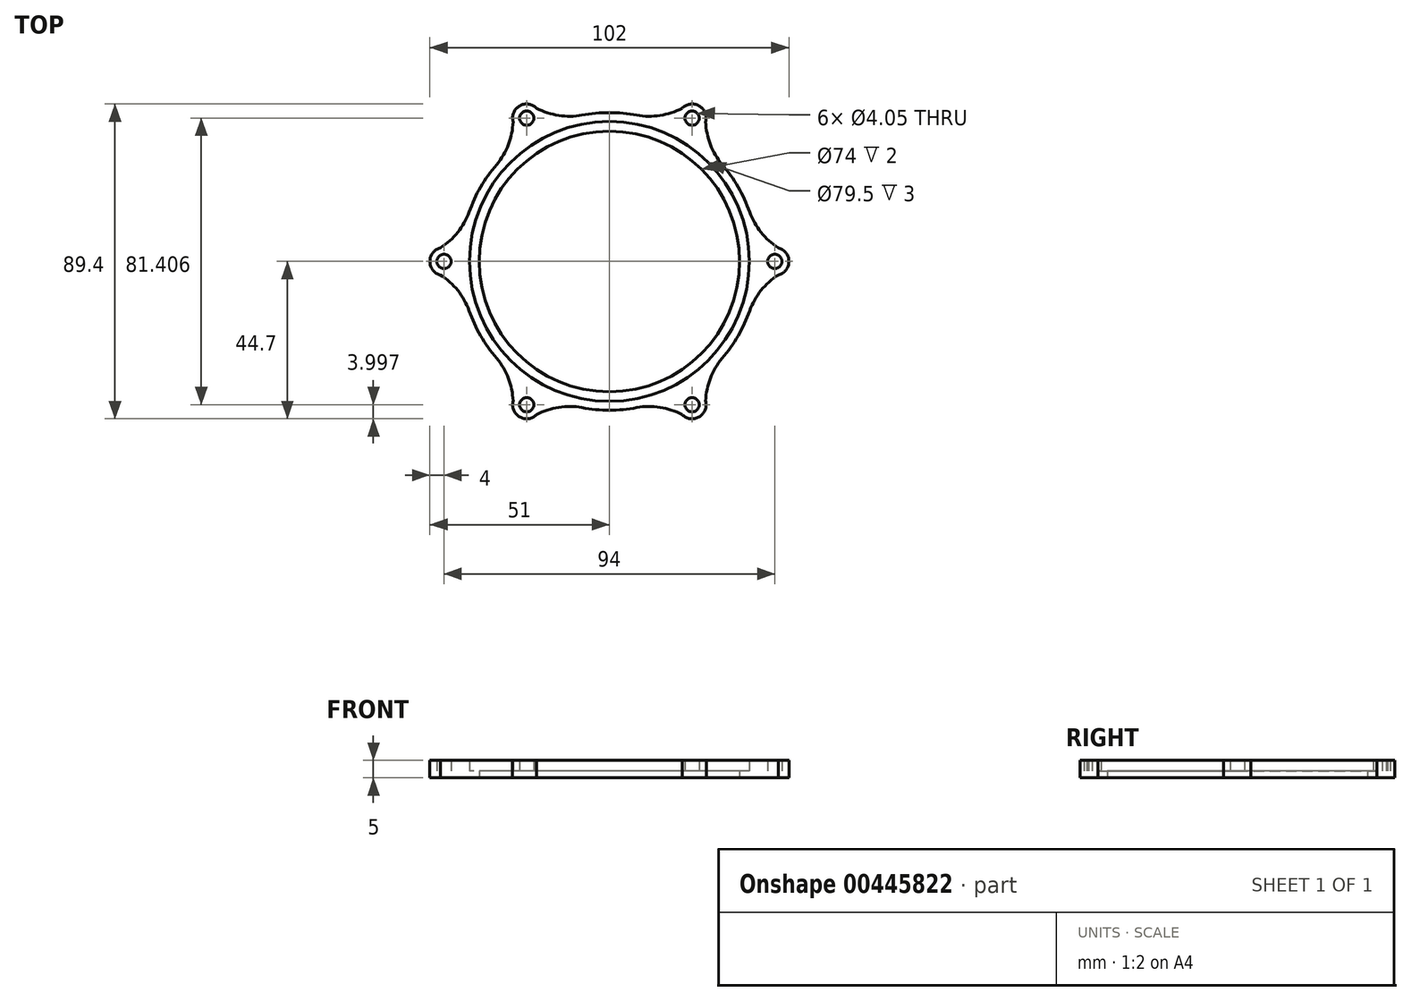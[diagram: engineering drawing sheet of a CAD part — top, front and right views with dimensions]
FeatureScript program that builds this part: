
annotation { "Feature Type Name" : "Feature", "Feature Type Description" : "" }
export const myFeature = defineFeature(function(context is Context, id is Id, definition is map)
    precondition{}
    {
        {
            var Q0;
            Q0=qCreatedBy(makeId("Top.planeOp"),FACE);
            var sketch = newSketch(context, id + "F0", { "sketchPlane" : qUnion([Q0])});
            skCircle(sketch, "E0", {"center": v(0, 0) * mm, "radius": 37 * mm});
            skCircle(sketch, "E1", {"center": v(0, 0) * mm, "radius": 39.75 * mm});
            skArc(sketch, "E2", {"start": v(-32.06, 27.52) * mm, "mid": v(-36.59, 21.12) * mm, "end": v(-39.86, 14) * mm});
            skArc(sketch, "E3", {"start": v(-48, 3.87) * mm, "mid": v(-51, 0) * mm, "end": v(-48, -3.87) * mm});
            skCircle(sketch, "E4", {"center": v(-47, 0) * mm, "radius": 2.02 * mm});
            skArc(sketch, "E5", {"start": v(-48, 3.87) * mm, "mid": v(-43.09, 8.26) * mm, "end": v(-39.86, 14) * mm});
            skArc(sketch, "E6.MirrorCS", {"start": v(-48, -3.87) * mm, "mid": v(-43.09, -8.26) * mm, "end": v(-39.86, -14) * mm});
            skArc(sketch, "E7.1.0", {"start": v(-27.35, -39.63) * mm, "mid": v(-28.7, -33.19) * mm, "end": v(-32.06, -27.52) * mm});
            skArc(sketch, "E7.1.1", {"start": v(-27.35, -39.63) * mm, "mid": v(-25.5, -44.17) * mm, "end": v(-20.65, -43.5) * mm});
            skCircle(sketch, "E7.1.2", {"center": v(-23.5, -40.7) * mm, "radius": 2.02 * mm});
            skArc(sketch, "E7.1.3", {"start": v(-20.65, -43.5) * mm, "mid": v(-14.4, -41.44) * mm, "end": v(-7.8, -41.52) * mm});
            skArc(sketch, "E7.2.0", {"start": v(20.65, -43.5) * mm, "mid": v(14.4, -41.44) * mm, "end": v(7.8, -41.52) * mm});
            skArc(sketch, "E7.2.1", {"start": v(20.65, -43.5) * mm, "mid": v(25.5, -44.17) * mm, "end": v(27.35, -39.63) * mm});
            skCircle(sketch, "E7.2.2", {"center": v(23.5, -40.7) * mm, "radius": 2.02 * mm});
            skArc(sketch, "E7.2.3", {"start": v(27.35, -39.63) * mm, "mid": v(28.7, -33.19) * mm, "end": v(32.06, -27.52) * mm});
            skArc(sketch, "E7.3.0", {"start": v(48, -3.87) * mm, "mid": v(43.09, -8.26) * mm, "end": v(39.86, -14) * mm});
            skArc(sketch, "E7.3.1", {"start": v(48, -3.87) * mm, "mid": v(51, 0) * mm, "end": v(48, 3.87) * mm});
            skCircle(sketch, "E7.3.2", {"center": v(47, 0) * mm, "radius": 2.02 * mm});
            skArc(sketch, "E7.3.3", {"start": v(48, 3.87) * mm, "mid": v(43.09, 8.26) * mm, "end": v(39.86, 14) * mm});
            skArc(sketch, "E7.4.0", {"start": v(27.35, 39.63) * mm, "mid": v(28.7, 33.19) * mm, "end": v(32.06, 27.52) * mm});
            skArc(sketch, "E7.4.1", {"start": v(27.35, 39.63) * mm, "mid": v(25.5, 44.17) * mm, "end": v(20.65, 43.5) * mm});
            skCircle(sketch, "E7.4.2", {"center": v(23.5, 40.7) * mm, "radius": 2.02 * mm});
            skArc(sketch, "E7.4.3", {"start": v(20.65, 43.5) * mm, "mid": v(14.4, 41.44) * mm, "end": v(7.8, 41.52) * mm});
            skArc(sketch, "E7.5.0", {"start": v(-20.65, 43.5) * mm, "mid": v(-14.4, 41.44) * mm, "end": v(-7.8, 41.52) * mm});
            skArc(sketch, "E7.5.1", {"start": v(-20.65, 43.5) * mm, "mid": v(-25.5, 44.17) * mm, "end": v(-27.35, 39.63) * mm});
            skCircle(sketch, "E7.5.2", {"center": v(-23.5, 40.7) * mm, "radius": 2.02 * mm});
            skArc(sketch, "E7.5.3", {"start": v(-27.35, 39.63) * mm, "mid": v(-28.7, 33.19) * mm, "end": v(-32.06, 27.52) * mm});
            skArc(sketch, "E8.trimOffspring", {"start": v(7.8, 41.52) * mm, "mid": v(0, 42.25) * mm, "end": v(-7.8, 41.52) * mm});
            skArc(sketch, "E9.trimOffspring", {"start": v(39.86, 14) * mm, "mid": v(36.59, 21.12) * mm, "end": v(32.06, 27.52) * mm});
            skArc(sketch, "E10.trimOffspring", {"start": v(32.06, -27.52) * mm, "mid": v(36.59, -21.13) * mm, "end": v(39.86, -14) * mm});
            skArc(sketch, "E11.trimOffspring", {"start": v(-7.8, -41.52) * mm, "mid": v(0, -42.25) * mm, "end": v(7.8, -41.52) * mm});
            skArc(sketch, "E12.trimOffspring", {"start": v(-39.86, -14) * mm, "mid": v(-36.59, -21.12) * mm, "end": v(-32.06, -27.52) * mm});
            skSolve(sketch);
        }
        {
            var Q0;
            Q0=makeQuery(id+"F0.imprint","IMPRINT",FACE,{"disambiguationData":[TD([[makeQuery(id+"F0.imprint","IMPRINT",EDGE,{"derivedFrom":sQuery(id+"F0.wireOp",EDGE,"E0")}),-1.0]])]});
            extrude(context, id + "F1", {"entities" : qUnion([Q0]), "depth" : 2 * mm});
        }
        {
            var Q0;
            Q0=makeQuery(id+"F0.imprint","IMPRINT",FACE,{"disambiguationData":[TD([[makeQuery(id+"F0.imprint","IMPRINT",EDGE,{"derivedFrom":sQuery(id+"F0.wireOp",EDGE,"E1")}),-1.0]])]});
            extrude(context, id + "F2", {"entities" : qUnion([Q0]), "operationType" : NewBodyOperationType.ADD, "depth" : 5 * mm});
        }
    });
